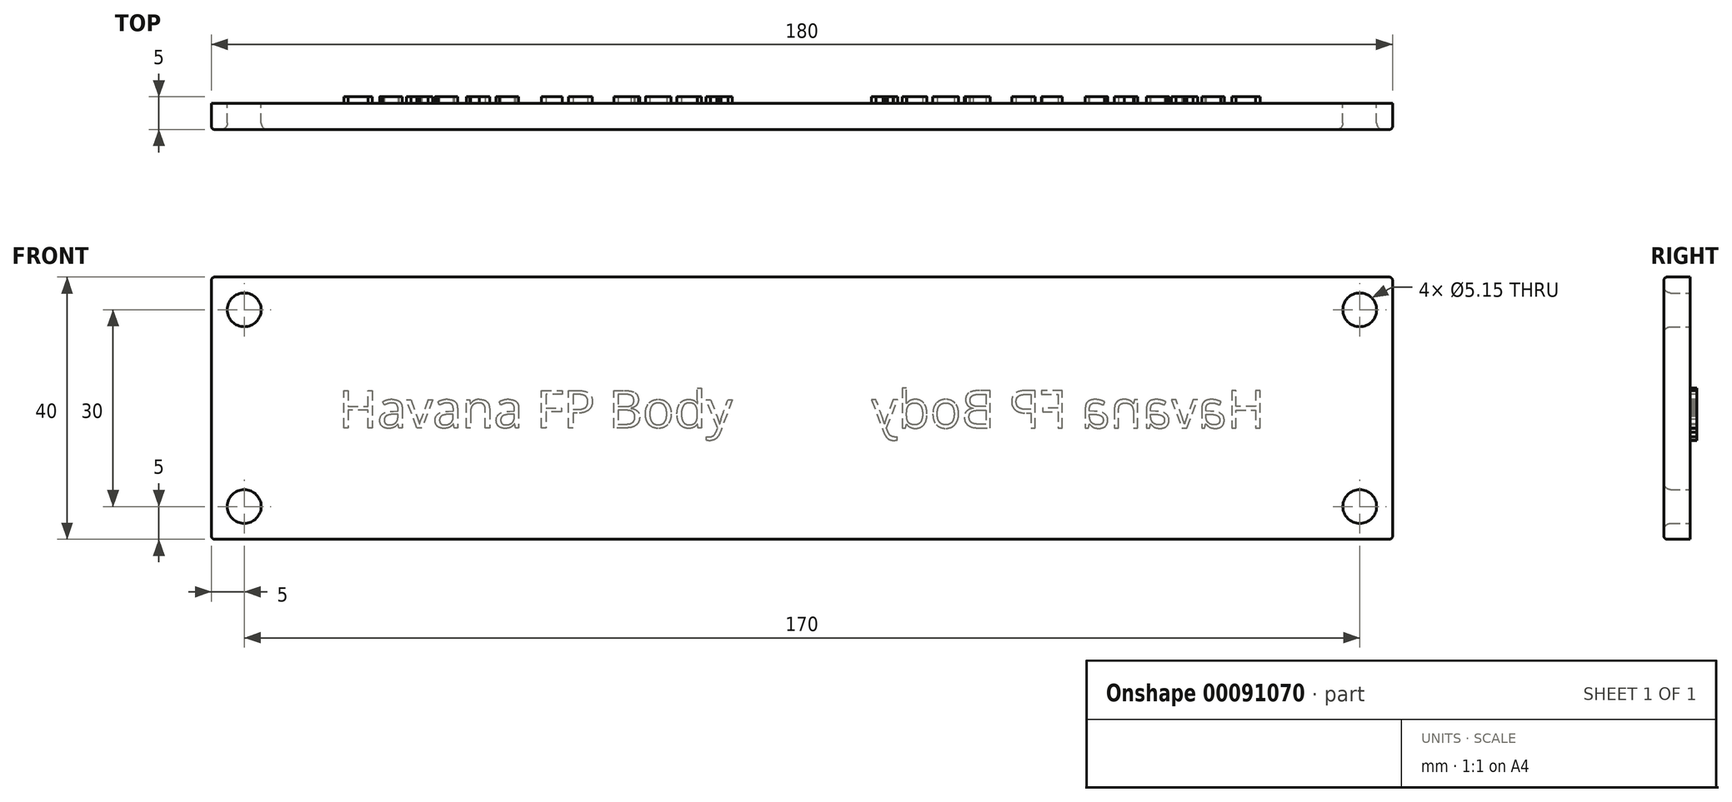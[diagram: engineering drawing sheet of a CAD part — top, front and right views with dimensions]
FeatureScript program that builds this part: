
annotation { "Feature Type Name" : "Feature", "Feature Type Description" : "" }
export const myFeature = defineFeature(function(context is Context, id is Id, definition is map)
    precondition{}
    {
        {
            var Q0;
            Q0=qCreatedBy(makeId("Front.planeOp"),FACE);
            var sketch = newSketch(context, id + "F0", { "sketchPlane" : qUnion([Q0])});
            skLineSegment(sketch, "E0.bottom", {"start": v(-90, -20) * mm, "end": v(90, -20) * mm});
            skLineSegment(sketch, "E0.top", {"start": v(-90, 20) * mm, "end": v(90, 20) * mm});
            skLineSegment(sketch, "E0.left", {"start": v(-90, -20) * mm, "end": v(-90, 20) * mm});
            skLineSegment(sketch, "E0.right", {"start": v(90, -20) * mm, "end": v(90, 20) * mm});
            skPoint(sketch, "E0.middle", {"position": v(0, 0) * mm});
            skCircle(sketch, "E1", {"center": v(-85, 15) * mm, "radius": 2.58 * mm});
            skPoint(sketch, "E2.start.orphan", {"position": v(-90, 0) * mm});
            skPoint(sketch, "E3.orphan", {"position": v(0, 20) * mm});
            skPoint(sketch, "E4.end.orphan", {"position": v(0, -20) * mm});
            skLineSegment(sketch, "E5", {"start": v(-90, 0) * mm, "end": v(0, 0) * mm, "construction": true});
            skLineSegment(sketch, "E6", {"start": v(0, 20) * mm, "end": v(0, -20) * mm, "construction": true});
            skCircle(sketch, "E7.MirrorC", {"center": v(-85, -15) * mm, "radius": 2.58 * mm});
            skCircle(sketch, "E8.MirrorC", {"center": v(85, 15) * mm, "radius": 2.58 * mm});
            skCircle(sketch, "E9.MirrorC", {"center": v(85, -15) * mm, "radius": 2.58 * mm});
            skSolve(sketch);
        }
        {
            var Q0;
            Q0=makeQuery(id+"F0.imprint","IMPRINT",FACE,{"disambiguationData":[TD([[makeQuery(id+"F0.imprint","IMPRINT",EDGE,{"derivedFrom":sQuery(id+"F0.wireOp",EDGE,"E0.bottom")}),1.0]])]});
            extrude(context, id + "F1", {"entities" : qUnion([Q0]), "depth" : 4 * mm});
        }
        {
            var Q0;
            Q0=makeQuery(id+"F1.opExtrude","CAP_EDGE",EDGE,{"disambiguationData":[OSD([sQuery(id+"F0.wireOp",EDGE,"E1")])],"isStart":false});
            var Q1;
            Q1=makeQuery(id+"F1.opExtrude","CAP_EDGE",EDGE,{"disambiguationData":[OSD([sQuery(id+"F0.wireOp",EDGE,"f5b72a5b-8583-449a-bdbf-9ac5a681e1fd0.MirrorC")])],"isStart":false});
            var Q2;
            Q2=makeQuery(id+"F1.opExtrude","CAP_EDGE",EDGE,{"disambiguationData":[OSD([sQuery(id+"F0.wireOp",EDGE,"2623e306-60f4-4522-aa65-1e3e8c2cf5b60.MirrorC")])],"isStart":false});
            var Q3;
            Q3=makeQuery(id+"F1.opExtrude","CAP_EDGE",EDGE,{"disambiguationData":[OSD([sQuery(id+"F0.wireOp",EDGE,"be81a34d-1d50-4ce7-a7a8-4484a1701fac0.MirrorC")])],"isStart":false});
            var Q4;
            Q4=makeQuery(id+"F1.opExtrude","CAP_EDGE",EDGE,{"disambiguationData":[OSD([sQuery(id+"F0.wireOp",EDGE,"E7.MirrorC")])],"isStart":false});
            var Q5;
            Q5=makeQuery(id+"F1.opExtrude","CAP_EDGE",EDGE,{"disambiguationData":[OSD([sQuery(id+"F0.wireOp",EDGE,"E8.MirrorC")])],"isStart":false});
            var Q6;
            Q6=makeQuery(id+"F1.opExtrude","CAP_EDGE",EDGE,{"disambiguationData":[OSD([sQuery(id+"F0.wireOp",EDGE,"E9.MirrorC")])],"isStart":false});
            fillet(context, id + "F2", {"entities" : qUnion([Q0, Q1, Q2, Q3, Q4, Q5, Q6]), "radius" : 1 * mm, "tangentPropagation" : true, "allowEdgeOverflow" : false});
        }
        {
            var Q0;
            Q0=makeQuery(id+"F1.opExtrude","CAP_EDGE",EDGE,{"disambiguationData":[OSD([sQuery(id+"F0.wireOp",EDGE,"E0.top")])],"isStart":false});
            var Q1;
            Q1=makeQuery(id+"F1.opExtrude","CAP_EDGE",EDGE,{"disambiguationData":[OSD([sQuery(id+"F0.wireOp",EDGE,"E0.left")])],"isStart":false});
            var Q2;
            Q2=makeQuery(id+"F1.opExtrude","CAP_EDGE",EDGE,{"disambiguationData":[OSD([sQuery(id+"F0.wireOp",EDGE,"E0.bottom")])],"isStart":false});
            var Q3;
            Q3=makeQuery(id+"F1.opExtrude","CAP_EDGE",EDGE,{"disambiguationData":[OSD([sQuery(id+"F0.wireOp",EDGE,"E0.right")])],"isStart":false});
            var Q4;
            Q4=makeQuery(id+"F1.opExtrude","SWEPT_EDGE",EDGE,{"disambiguationData":[OSD([sQuery(id+"F0.wireOp",EDGE,"E0.top"),sQuery(id+"F0.wireOp",EDGE,"E0.left")])]});
            var Q5;
            Q5=makeQuery(id+"F1.opExtrude","SWEPT_EDGE",EDGE,{"disambiguationData":[OSD([sQuery(id+"F0.wireOp",EDGE,"E0.bottom"),sQuery(id+"F0.wireOp",EDGE,"E0.left")])]});
            var Q6;
            Q6=makeQuery(id+"F1.opExtrude","SWEPT_EDGE",EDGE,{"disambiguationData":[OSD([sQuery(id+"F0.wireOp",EDGE,"E0.top"),sQuery(id+"F0.wireOp",EDGE,"E0.right")])]});
            var Q7;
            Q7=makeQuery(id+"F1.opExtrude","SWEPT_EDGE",EDGE,{"disambiguationData":[OSD([sQuery(id+"F0.wireOp",EDGE,"E0.bottom"),sQuery(id+"F0.wireOp",EDGE,"E0.right")])]});
            fillet(context, id + "F3", {"entities" : qUnion([Q0, Q1, Q2, Q3, Q4, Q5, Q6, Q7]), "radius" : .5 * mm, "tangentPropagation" : true, "allowEdgeOverflow" : false});
        }
        {
            var Q0;
            Q0=makeQuery(id+"F1.opExtrude","CAP_FACE",FACE,{"disambiguationData":[OSD([sQuery(id+"F0.wireOp",EDGE,"E0.bottom"),sQuery(id+"F0.wireOp",EDGE,"E0.top"),sQuery(id+"F0.wireOp",EDGE,"E0.left"),sQuery(id+"F0.wireOp",EDGE,"E0.right"),sQuery(id+"F0.wireOp",EDGE,"E1"),sQuery(id+"F0.wireOp",EDGE,"E7.MirrorC"),sQuery(id+"F0.wireOp",EDGE,"E8.MirrorC"),sQuery(id+"F0.wireOp",EDGE,"E9.MirrorC")])],"isStart":true});
            var sketch = newSketch(context, id + "F4", { "sketchPlane" : qUnion([Q0])});
            skText(sketch, "E10", { "text": "Havana FP Body", "fontName": "OpenSans-Regular.ttf"});
            skLineSegment(sketch, "E11", {"start": v(0, 20) * mm, "end": v(0, -20) * mm, "construction": true});
            const initialGuessF4  = {"E10": [-0.0706, -0.003, 1, 0, 0.00574]};
            skSetInitialGuess(sketch, initialGuessF4);
            skSolve(sketch);
        }
        {
            var Q0;
            Q0=qSketchRegion(id+"F4",true);
            extrude(context, id + "F5", {"entities" : qUnion([Q0]), "operationType" : NewBodyOperationType.ADD, "depth" : 1 * mm});
        }
        {
            var Q0;
            Q0=makeQuery(id+"F1.opExtrude","SWEPT_BODY",BODY,{"disambiguationData":[OSD([sQuery(id+"F0.wireOp",EDGE,"E0.bottom"),sQuery(id+"F0.wireOp",EDGE,"E0.top"),sQuery(id+"F0.wireOp",EDGE,"E0.left"),sQuery(id+"F0.wireOp",EDGE,"E0.right"),sQuery(id+"F0.wireOp",EDGE,"E1"),sQuery(id+"F0.wireOp",EDGE,"E7.MirrorC"),sQuery(id+"F0.wireOp",EDGE,"E8.MirrorC"),sQuery(id+"F0.wireOp",EDGE,"E9.MirrorC")])]});
            var Q1;
            Q1=makeQuery(id+"F5.opExtrude","SWEPT_FACE",FACE,{"disambiguationData":[OSD([sQuery(id+"F4.wireOp",EDGE,"E10.sketch_text.stroke-94")])]});
            var Q2;
            Q2=makeQuery(id+"F5.opExtrude","SWEPT_FACE",FACE,{"disambiguationData":[OSD([sQuery(id+"F4.wireOp",EDGE,"E10.sketch_text.stroke-169")])]});
            var Q3;
            Q3=makeQuery(id+"F5.opExtrude","SWEPT_FACE",FACE,{"disambiguationData":[OSD([sQuery(id+"F4.wireOp",EDGE,"E10.sketch_text.stroke-185")])]});
            var Q4;
            Q4=makeQuery(id+"F5.opExtrude","SWEPT_FACE",FACE,{"disambiguationData":[OSD([sQuery(id+"F4.wireOp",EDGE,"E10.sketch_text.stroke-125")])]});
            var Q5;
            Q5=makeQuery(id+"F5.opExtrude","SWEPT_FACE",FACE,{"disambiguationData":[OSD([sQuery(id+"F4.wireOp",EDGE,"E10.sketch_text.stroke-155")])]});
            var Q6;
            Q6=makeQuery(id+"F5.opExtrude","SWEPT_FACE",FACE,{"disambiguationData":[OSD([sQuery(id+"F4.wireOp",EDGE,"E10.sketch_text.stroke-65")])]});
            var Q7;
            Q7=makeQuery(id+"F5.opExtrude","SWEPT_FACE",FACE,{"disambiguationData":[OSD([sQuery(id+"F4.wireOp",EDGE,"E10.sketch_text.stroke-81")])]});
            var Q8;
            Q8=makeQuery(id+"F5.opExtrude","SWEPT_FACE",FACE,{"disambiguationData":[OSD([sQuery(id+"F4.wireOp",EDGE,"E10.sketch_text.stroke-67")])]});
            var Q9;
            Q9=makeQuery(id+"F5.opExtrude","SWEPT_FACE",FACE,{"disambiguationData":[OSD([sQuery(id+"F4.wireOp",EDGE,"E10.sketch_text.stroke-99")])]});
            var Q10;
            Q10=makeQuery(id+"F5.opExtrude","SWEPT_FACE",FACE,{"disambiguationData":[OSD([sQuery(id+"F4.wireOp",EDGE,"E10.sketch_text.stroke-127")])]});
            var Q11;
            Q11=makeQuery(id+"F5.opExtrude","SWEPT_FACE",FACE,{"disambiguationData":[OSD([sQuery(id+"F4.wireOp",EDGE,"E10.sketch_text.stroke-10")])]});
            var Q12;
            Q12=makeQuery(id+"F5.opExtrude","CAP_FACE",FACE,{"disambiguationData":[OSD([sQuery(id+"F4.wireOp",EDGE,"E10.sketch_text.stroke-9"),sQuery(id+"F4.wireOp",EDGE,"E10.sketch_text.stroke-10"),sQuery(id+"F4.wireOp",EDGE,"E10.sketch_text.stroke-11"),sQuery(id+"F4.wireOp",EDGE,"E10.sketch_text.stroke-12")])],"isStart":false});
            var Q13;
            Q13=makeQuery(id+"F5.opExtrude","SWEPT_FACE",FACE,{"disambiguationData":[OSD([sQuery(id+"F4.wireOp",EDGE,"E10.sketch_text.stroke-154")])]});
            var Q14;
            Q14=makeQuery(id+"F5.opExtrude","SWEPT_FACE",FACE,{"disambiguationData":[OSD([sQuery(id+"F4.wireOp",EDGE,"E10.sketch_text.stroke-1")])]});
            var Q15;
            Q15=makeQuery(id+"F5.opExtrude","CAP_FACE",FACE,{"disambiguationData":[OSD([sQuery(id+"F4.wireOp",EDGE,"E10.sketch_text.stroke-124"),sQuery(id+"F4.wireOp",EDGE,"E10.sketch_text.stroke-125"),sQuery(id+"F4.wireOp",EDGE,"E10.sketch_text.stroke-126"),sQuery(id+"F4.wireOp",EDGE,"E10.sketch_text.stroke-127"),sQuery(id+"F4.wireOp",EDGE,"E10.sketch_text.stroke-128"),sQuery(id+"F4.wireOp",EDGE,"E10.sketch_text.stroke-129"),sQuery(id+"F4.wireOp",EDGE,"E10.sketch_text.stroke-130"),sQuery(id+"F4.wireOp",EDGE,"E10.sketch_text.stroke-131"),sQuery(id+"F4.wireOp",EDGE,"E10.sketch_text.stroke-132"),sQuery(id+"F4.wireOp",EDGE,"E10.sketch_text.stroke-133"),sQuery(id+"F4.wireOp",EDGE,"E10.sketch_text.stroke-134"),sQuery(id+"F4.wireOp",EDGE,"E10.sketch_text.stroke-135"),sQuery(id+"F4.wireOp",EDGE,"E10.sketch_text.stroke-136"),sQuery(id+"F4.wireOp",EDGE,"E10.sketch_text.stroke-137"),sQuery(id+"F4.wireOp",EDGE,"E10.sketch_text.stroke-138")])],"isStart":false});
            var Q16;
            Q16=makeQuery(id+"F5.opExtrude","CAP_FACE",FACE,{"disambiguationData":[OSD([sQuery(id+"F4.wireOp",EDGE,"E10.sketch_text.stroke-34"),sQuery(id+"F4.wireOp",EDGE,"E10.sketch_text.stroke-35"),sQuery(id+"F4.wireOp",EDGE,"E10.sketch_text.stroke-36"),sQuery(id+"F4.wireOp",EDGE,"E10.sketch_text.stroke-37"),sQuery(id+"F4.wireOp",EDGE,"E10.sketch_text.stroke-38"),sQuery(id+"F4.wireOp",EDGE,"E10.sketch_text.stroke-39"),sQuery(id+"F4.wireOp",EDGE,"E10.sketch_text.stroke-40"),sQuery(id+"F4.wireOp",EDGE,"E10.sketch_text.stroke-41"),sQuery(id+"F4.wireOp",EDGE,"E10.sketch_text.stroke-42"),sQuery(id+"F4.wireOp",EDGE,"E10.sketch_text.stroke-43"),sQuery(id+"F4.wireOp",EDGE,"E10.sketch_text.stroke-44"),sQuery(id+"F4.wireOp",EDGE,"E10.sketch_text.stroke-45"),sQuery(id+"F4.wireOp",EDGE,"E10.sketch_text.stroke-46"),sQuery(id+"F4.wireOp",EDGE,"E10.sketch_text.stroke-47"),sQuery(id+"F4.wireOp",EDGE,"E10.sketch_text.stroke-48"),sQuery(id+"F4.wireOp",EDGE,"E10.sketch_text.stroke-49"),sQuery(id+"F4.wireOp",EDGE,"E10.sketch_text.stroke-50"),sQuery(id+"F4.wireOp",EDGE,"E10.sketch_text.stroke-51"),sQuery(id+"F4.wireOp",EDGE,"E10.sketch_text.stroke-52"),sQuery(id+"F4.wireOp",EDGE,"E10.sketch_text.stroke-53"),sQuery(id+"F4.wireOp",EDGE,"E10.sketch_text.stroke-54"),sQuery(id+"F4.wireOp",EDGE,"E10.sketch_text.stroke-55"),sQuery(id+"F4.wireOp",EDGE,"E10.sketch_text.stroke-56"),sQuery(id+"F4.wireOp",EDGE,"E10.sketch_text.stroke-57"),sQuery(id+"F4.wireOp",EDGE,"E10.sketch_text.stroke-58"),sQuery(id+"F4.wireOp",EDGE,"E10.sketch_text.stroke-59"),sQuery(id+"F4.wireOp",EDGE,"E10.sketch_text.stroke-60")])],"isStart":false});
            var Q17;
            Q17=makeQuery(id+"F5.opExtrude","SWEPT_FACE",FACE,{"disambiguationData":[OSD([sQuery(id+"F4.wireOp",EDGE,"E10.sketch_text.stroke-50")])]});
            var Q18;
            Q18=makeQuery(id+"F5.opExtrude","SWEPT_FACE",FACE,{"disambiguationData":[OSD([sQuery(id+"F4.wireOp",EDGE,"E10.sketch_text.stroke-2")])]});
            var Q19;
            Q19=makeQuery(id+"F5.opExtrude","SWEPT_FACE",FACE,{"disambiguationData":[OSD([sQuery(id+"F4.wireOp",EDGE,"E10.sketch_text.stroke-3")])]});
            var Q20;
            Q20=makeQuery(id+"F5.opExtrude","SWEPT_FACE",FACE,{"disambiguationData":[OSD([sQuery(id+"F4.wireOp",EDGE,"E10.sketch_text.stroke-5")])]});
            var Q21;
            Q21=makeQuery(id+"F5.opExtrude","SWEPT_FACE",FACE,{"disambiguationData":[OSD([sQuery(id+"F4.wireOp",EDGE,"E10.sketch_text.stroke-8")])]});
            var Q22;
            Q22=makeQuery(id+"F5.opExtrude","SWEPT_FACE",FACE,{"disambiguationData":[OSD([sQuery(id+"F4.wireOp",EDGE,"E10.sketch_text.stroke-98")])]});
            var Q23;
            Q23=makeQuery(id+"F5.opExtrude","SWEPT_FACE",FACE,{"disambiguationData":[OSD([sQuery(id+"F4.wireOp",EDGE,"E10.sketch_text.stroke-66")])]});
            var Q24;
            Q24=makeQuery(id+"F5.opExtrude","SWEPT_FACE",FACE,{"disambiguationData":[OSD([sQuery(id+"F4.wireOp",EDGE,"E10.sketch_text.stroke-153")])]});
            var Q25;
            Q25=makeQuery(id+"F5.opExtrude","SWEPT_FACE",FACE,{"disambiguationData":[OSD([sQuery(id+"F4.wireOp",EDGE,"E10.sketch_text.stroke-126")])]});
            var Q26;
            Q26=makeQuery(id+"F5.opExtrude","SWEPT_FACE",FACE,{"disambiguationData":[OSD([sQuery(id+"F4.wireOp",EDGE,"E10.sketch_text.stroke-183")])]});
            var Q27;
            Q27=makeQuery(id+"F5.opExtrude","SWEPT_FACE",FACE,{"disambiguationData":[OSD([sQuery(id+"F4.wireOp",EDGE,"E10.sketch_text.stroke-109")])]});
            var Q28;
            Q28=makeQuery(id+"F5.opExtrude","SWEPT_FACE",FACE,{"disambiguationData":[OSD([sQuery(id+"F4.wireOp",EDGE,"E10.sketch_text.stroke-186")])]});
            var Q29;
            Q29=makeQuery(id+"F5.opExtrude","SWEPT_FACE",FACE,{"disambiguationData":[OSD([sQuery(id+"F4.wireOp",EDGE,"E10.sketch_text.stroke-79")])]});
            var Q30;
            Q30=makeQuery(id+"F5.opExtrude","SWEPT_FACE",FACE,{"disambiguationData":[OSD([sQuery(id+"F4.wireOp",EDGE,"E10.sketch_text.stroke-110")])]});
            var Q31;
            Q31=makeQuery(id+"F5.opExtrude","SWEPT_FACE",FACE,{"disambiguationData":[OSD([sQuery(id+"F4.wireOp",EDGE,"E10.sketch_text.stroke-38")])]});
            var Q32;
            Q32=makeQuery(id+"F5.opExtrude","SWEPT_FACE",FACE,{"disambiguationData":[OSD([sQuery(id+"F4.wireOp",EDGE,"E10.sketch_text.stroke-24")])]});
            var Q33;
            Q33=makeQuery(id+"F5.opExtrude","SWEPT_FACE",FACE,{"disambiguationData":[OSD([sQuery(id+"F4.wireOp",EDGE,"E10.sketch_text.stroke-12")])]});
            var Q34;
            Q34=makeQuery(id+"F5.opExtrude","SWEPT_FACE",FACE,{"disambiguationData":[OSD([sQuery(id+"F4.wireOp",EDGE,"E10.sketch_text.stroke-100")])]});
            var Q35;
            Q35=makeQuery(id+"F5.opExtrude","SWEPT_FACE",FACE,{"disambiguationData":[OSD([sQuery(id+"F4.wireOp",EDGE,"E10.sketch_text.stroke-158")])]});
            var Q36;
            Q36=makeQuery(id+"F5.opExtrude","SWEPT_FACE",FACE,{"disambiguationData":[OSD([sQuery(id+"F4.wireOp",EDGE,"E10.sketch_text.stroke-142")])]});
            var Q37;
            Q37=makeQuery(id+"F5.opExtrude","SWEPT_FACE",FACE,{"disambiguationData":[OSD([sQuery(id+"F4.wireOp",EDGE,"E10.sketch_text.stroke-54")])]});
            var Q38;
            Q38=makeQuery(id+"F5.opExtrude","SWEPT_FACE",FACE,{"disambiguationData":[OSD([sQuery(id+"F4.wireOp",EDGE,"E10.sketch_text.stroke-25")])]});
            var Q39;
            Q39=makeQuery(id+"F5.opExtrude","SWEPT_FACE",FACE,{"disambiguationData":[OSD([sQuery(id+"F4.wireOp",EDGE,"E10.sketch_text.stroke-101")])]});
            var Q40;
            Q40=makeQuery(id+"F5.opExtrude","SWEPT_FACE",FACE,{"disambiguationData":[OSD([sQuery(id+"F4.wireOp",EDGE,"E10.sketch_text.stroke-69")])]});
            var Q41;
            Q41=makeQuery(id+"F5.opExtrude","SWEPT_FACE",FACE,{"disambiguationData":[OSD([sQuery(id+"F4.wireOp",EDGE,"E10.sketch_text.stroke-159")])]});
            var Q42;
            Q42=makeQuery(id+"F5.opExtrude","SWEPT_FACE",FACE,{"disambiguationData":[OSD([sQuery(id+"F4.wireOp",EDGE,"E10.sketch_text.stroke-85")])]});
            var Q43;
            Q43=makeQuery(id+"F5.opExtrude","SWEPT_FACE",FACE,{"disambiguationData":[OSD([sQuery(id+"F4.wireOp",EDGE,"E10.sketch_text.stroke-173")])]});
            var Q44;
            Q44=makeQuery(id+"F5.opExtrude","SWEPT_FACE",FACE,{"disambiguationData":[OSD([sQuery(id+"F4.wireOp",EDGE,"E10.sketch_text.stroke-40")])]});
            var Q45;
            Q45=makeQuery(id+"F5.opExtrude","SWEPT_FACE",FACE,{"disambiguationData":[OSD([sQuery(id+"F4.wireOp",EDGE,"E10.sketch_text.stroke-102")])]});
            var Q46;
            Q46=makeQuery(id+"F5.opExtrude","SWEPT_FACE",FACE,{"disambiguationData":[OSD([sQuery(id+"F4.wireOp",EDGE,"E10.sketch_text.stroke-86")])]});
            var Q47;
            Q47=makeQuery(id+"F5.opExtrude","SWEPT_FACE",FACE,{"disambiguationData":[OSD([sQuery(id+"F4.wireOp",EDGE,"E10.sketch_text.stroke-130")])]});
            var Q48;
            Q48=makeQuery(id+"F5.opExtrude","SWEPT_FACE",FACE,{"disambiguationData":[OSD([sQuery(id+"F4.wireOp",EDGE,"E10.sketch_text.stroke-103")])]});
            var Q49;
            Q49=makeQuery(id+"F5.opExtrude","SWEPT_FACE",FACE,{"disambiguationData":[OSD([sQuery(id+"F4.wireOp",EDGE,"E10.sketch_text.stroke-87")])]});
            var Q50;
            Q50=makeQuery(id+"F5.opExtrude","SWEPT_FACE",FACE,{"disambiguationData":[OSD([sQuery(id+"F4.wireOp",EDGE,"E10.sketch_text.stroke-145")])]});
            var Q51;
            Q51=makeQuery(id+"F5.opExtrude","SWEPT_FACE",FACE,{"disambiguationData":[OSD([sQuery(id+"F4.wireOp",EDGE,"E10.sketch_text.stroke-131")])]});
            var Q52;
            Q52=makeQuery(id+"F5.opExtrude","SWEPT_FACE",FACE,{"disambiguationData":[OSD([sQuery(id+"F4.wireOp",EDGE,"E10.sketch_text.stroke-28")])]});
            var Q53;
            Q53=makeQuery(id+"F5.opExtrude","SWEPT_FACE",FACE,{"disambiguationData":[OSD([sQuery(id+"F4.wireOp",EDGE,"E10.sketch_text.stroke-14")])]});
            var Q54;
            Q54=makeQuery(id+"F5.opExtrude","SWEPT_FACE",FACE,{"disambiguationData":[OSD([sQuery(id+"F4.wireOp",EDGE,"E10.sketch_text.stroke-88")])]});
            var Q55;
            Q55=makeQuery(id+"F5.opExtrude","SWEPT_FACE",FACE,{"disambiguationData":[OSD([sQuery(id+"F4.wireOp",EDGE,"E10.sketch_text.stroke-162")])]});
            var Q56;
            Q56=makeQuery(id+"F5.opExtrude","SWEPT_FACE",FACE,{"disambiguationData":[OSD([sQuery(id+"F4.wireOp",EDGE,"E10.sketch_text.stroke-176")])]});
            var Q57;
            Q57=makeQuery(id+"F5.opExtrude","SWEPT_FACE",FACE,{"disambiguationData":[OSD([sQuery(id+"F4.wireOp",EDGE,"E10.sketch_text.stroke-73")])]});
            var Q58;
            Q58=makeQuery(id+"F5.opExtrude","SWEPT_FACE",FACE,{"disambiguationData":[OSD([sQuery(id+"F4.wireOp",EDGE,"E10.sketch_text.stroke-59")])]});
            var Q59;
            Q59=makeQuery(id+"F5.opExtrude","SWEPT_FACE",FACE,{"disambiguationData":[OSD([sQuery(id+"F4.wireOp",EDGE,"E10.sketch_text.stroke-133")])]});
            var Q60;
            Q60=makeQuery(id+"F5.opExtrude","SWEPT_FACE",FACE,{"disambiguationData":[OSD([sQuery(id+"F4.wireOp",EDGE,"E10.sketch_text.stroke-119")])]});
            var Q61;
            Q61=makeQuery(id+"F5.opExtrude","SWEPT_FACE",FACE,{"disambiguationData":[OSD([sQuery(id+"F4.wireOp",EDGE,"E10.sketch_text.stroke-74")])]});
            var Q62;
            Q62=makeQuery(id+"F5.opExtrude","SWEPT_FACE",FACE,{"disambiguationData":[OSD([sQuery(id+"F4.wireOp",EDGE,"E10.sketch_text.stroke-44")])]});
            var Q63;
            Q63=makeQuery(id+"F5.opExtrude","SWEPT_FACE",FACE,{"disambiguationData":[OSD([sQuery(id+"F4.wireOp",EDGE,"E10.sketch_text.stroke-120")])]});
            var Q64;
            Q64=makeQuery(id+"F5.opExtrude","SWEPT_FACE",FACE,{"disambiguationData":[OSD([sQuery(id+"F4.wireOp",EDGE,"E10.sketch_text.stroke-90")])]});
            var Q65;
            Q65=makeQuery(id+"F5.opExtrude","SWEPT_FACE",FACE,{"disambiguationData":[OSD([sQuery(id+"F4.wireOp",EDGE,"E10.sketch_text.stroke-178")])]});
            var Q66;
            Q66=makeQuery(id+"F5.opExtrude","SWEPT_FACE",FACE,{"disambiguationData":[OSD([sQuery(id+"F4.wireOp",EDGE,"E10.sketch_text.stroke-45")])]});
            var Q67;
            Q67=makeQuery(id+"F5.opExtrude","SWEPT_FACE",FACE,{"disambiguationData":[OSD([sQuery(id+"F4.wireOp",EDGE,"E10.sketch_text.stroke-31")])]});
            var Q68;
            Q68=makeQuery(id+"F5.opExtrude","SWEPT_FACE",FACE,{"disambiguationData":[OSD([sQuery(id+"F4.wireOp",EDGE,"E10.sketch_text.stroke-135")])]});
            var Q69;
            Q69=makeQuery(id+"F5.opExtrude","SWEPT_FACE",FACE,{"disambiguationData":[OSD([sQuery(id+"F4.wireOp",EDGE,"E10.sketch_text.stroke-179")])]});
            var Q70;
            Q70=makeQuery(id+"F5.opExtrude","SWEPT_FACE",FACE,{"disambiguationData":[OSD([sQuery(id+"F4.wireOp",EDGE,"E10.sketch_text.stroke-165")])]});
            var Q71;
            Q71=makeQuery(id+"F5.opExtrude","SWEPT_FACE",FACE,{"disambiguationData":[OSD([sQuery(id+"F4.wireOp",EDGE,"E10.sketch_text.stroke-149")])]});
            var Q72;
            Q72=makeQuery(id+"F5.opExtrude","SWEPT_FACE",FACE,{"disambiguationData":[OSD([sQuery(id+"F4.wireOp",EDGE,"E10.sketch_text.stroke-136")])]});
            var Q73;
            Q73=makeQuery(id+"F5.opExtrude","SWEPT_FACE",FACE,{"disambiguationData":[OSD([sQuery(id+"F4.wireOp",EDGE,"E10.sketch_text.stroke-122")])]});
            var Q74;
            Q74=makeQuery(id+"F5.opExtrude","SWEPT_FACE",FACE,{"disambiguationData":[OSD([sQuery(id+"F4.wireOp",EDGE,"E10.sketch_text.stroke-106")])]});
            var Q75;
            Q75=makeQuery(id+"F5.opExtrude","SWEPT_FACE",FACE,{"disambiguationData":[OSD([sQuery(id+"F4.wireOp",EDGE,"E10.sketch_text.stroke-180")])]});
            var Q76;
            Q76=makeQuery(id+"F5.opExtrude","SWEPT_FACE",FACE,{"disambiguationData":[OSD([sQuery(id+"F4.wireOp",EDGE,"E10.sketch_text.stroke-166")])]});
            var Q77;
            Q77=makeQuery(id+"F5.opExtrude","SWEPT_FACE",FACE,{"disambiguationData":[OSD([sQuery(id+"F4.wireOp",EDGE,"E10.sketch_text.stroke-150")])]});
            var Q78;
            Q78=makeQuery(id+"F5.opExtrude","SWEPT_FACE",FACE,{"disambiguationData":[OSD([sQuery(id+"F4.wireOp",EDGE,"E10.sketch_text.stroke-76")])]});
            var Q79;
            Q79=makeQuery(id+"F5.opExtrude","SWEPT_FACE",FACE,{"disambiguationData":[OSD([sQuery(id+"F4.wireOp",EDGE,"E10.sketch_text.stroke-32")])]});
            var Q80;
            Q80=makeQuery(id+"F5.opExtrude","SWEPT_FACE",FACE,{"disambiguationData":[OSD([sQuery(id+"F4.wireOp",EDGE,"E10.sketch_text.stroke-181")])]});
            var Q81;
            Q81=makeQuery(id+"F5.opExtrude","SWEPT_FACE",FACE,{"disambiguationData":[OSD([sQuery(id+"F4.wireOp",EDGE,"E10.sketch_text.stroke-47")])]});
            var Q82;
            Q82=makeQuery(id+"F5.opExtrude","SWEPT_FACE",FACE,{"disambiguationData":[OSD([sQuery(id+"F4.wireOp",EDGE,"E10.sketch_text.stroke-123")])]});
            var Q83;
            Q83=makeQuery(id+"F5.opExtrude","SWEPT_FACE",FACE,{"disambiguationData":[OSD([sQuery(id+"F4.wireOp",EDGE,"E10.sketch_text.stroke-107")])]});
            var Q84;
            Q84=makeQuery(id+"F5.opExtrude","SWEPT_FACE",FACE,{"disambiguationData":[OSD([sQuery(id+"F4.wireOp",EDGE,"E10.sketch_text.stroke-48")])]});
            var Q85;
            Q85=makeQuery(id+"F5.opExtrude","SWEPT_FACE",FACE,{"disambiguationData":[OSD([sQuery(id+"F4.wireOp",EDGE,"E10.sketch_text.stroke-124")])]});
            var Q86;
            Q86=makeQuery(id+"F5.opExtrude","SWEPT_FACE",FACE,{"disambiguationData":[OSD([sQuery(id+"F4.wireOp",EDGE,"E10.sketch_text.stroke-108")])]});
            var Q87;
            Q87=makeQuery(id+"F5.opExtrude","CAP_FACE",FACE,{"disambiguationData":[OSD([sQuery(id+"F4.wireOp",EDGE,"E10.sketch_text.stroke-139"),sQuery(id+"F4.wireOp",EDGE,"E10.sketch_text.stroke-140"),sQuery(id+"F4.wireOp",EDGE,"E10.sketch_text.stroke-141"),sQuery(id+"F4.wireOp",EDGE,"E10.sketch_text.stroke-142"),sQuery(id+"F4.wireOp",EDGE,"E10.sketch_text.stroke-143"),sQuery(id+"F4.wireOp",EDGE,"E10.sketch_text.stroke-144"),sQuery(id+"F4.wireOp",EDGE,"E10.sketch_text.stroke-145"),sQuery(id+"F4.wireOp",EDGE,"E10.sketch_text.stroke-146"),sQuery(id+"F4.wireOp",EDGE,"E10.sketch_text.stroke-147"),sQuery(id+"F4.wireOp",EDGE,"E10.sketch_text.stroke-148"),sQuery(id+"F4.wireOp",EDGE,"E10.sketch_text.stroke-149"),sQuery(id+"F4.wireOp",EDGE,"E10.sketch_text.stroke-150"),sQuery(id+"F4.wireOp",EDGE,"E10.sketch_text.stroke-151"),sQuery(id+"F4.wireOp",EDGE,"E10.sketch_text.stroke-152"),sQuery(id+"F4.wireOp",EDGE,"E10.sketch_text.stroke-153"),sQuery(id+"F4.wireOp",EDGE,"E10.sketch_text.stroke-154"),sQuery(id+"F4.wireOp",EDGE,"E10.sketch_text.stroke-155"),sQuery(id+"F4.wireOp",EDGE,"E10.sketch_text.stroke-156"),sQuery(id+"F4.wireOp",EDGE,"E10.sketch_text.stroke-157"),sQuery(id+"F4.wireOp",EDGE,"E10.sketch_text.stroke-158"),sQuery(id+"F4.wireOp",EDGE,"E10.sketch_text.stroke-159"),sQuery(id+"F4.wireOp",EDGE,"E10.sketch_text.stroke-160"),sQuery(id+"F4.wireOp",EDGE,"E10.sketch_text.stroke-161"),sQuery(id+"F4.wireOp",EDGE,"E10.sketch_text.stroke-162"),sQuery(id+"F4.wireOp",EDGE,"E10.sketch_text.stroke-163"),sQuery(id+"F4.wireOp",EDGE,"E10.sketch_text.stroke-164"),sQuery(id+"F4.wireOp",EDGE,"E10.sketch_text.stroke-165")])],"isStart":false});
            var Q88;
            Q88=makeQuery(id+"F5.opExtrude","CAP_FACE",FACE,{"disambiguationData":[OSD([sQuery(id+"F4.wireOp",EDGE,"E10.sketch_text.stroke-21"),sQuery(id+"F4.wireOp",EDGE,"E10.sketch_text.stroke-22"),sQuery(id+"F4.wireOp",EDGE,"E10.sketch_text.stroke-23"),sQuery(id+"F4.wireOp",EDGE,"E10.sketch_text.stroke-24"),sQuery(id+"F4.wireOp",EDGE,"E10.sketch_text.stroke-25"),sQuery(id+"F4.wireOp",EDGE,"E10.sketch_text.stroke-26"),sQuery(id+"F4.wireOp",EDGE,"E10.sketch_text.stroke-27"),sQuery(id+"F4.wireOp",EDGE,"E10.sketch_text.stroke-28"),sQuery(id+"F4.wireOp",EDGE,"E10.sketch_text.stroke-29"),sQuery(id+"F4.wireOp",EDGE,"E10.sketch_text.stroke-30"),sQuery(id+"F4.wireOp",EDGE,"E10.sketch_text.stroke-31"),sQuery(id+"F4.wireOp",EDGE,"E10.sketch_text.stroke-32"),sQuery(id+"F4.wireOp",EDGE,"E10.sketch_text.stroke-33")])],"isStart":false});
            var Q89;
            Q89=makeQuery(id+"F5.opExtrude","SWEPT_FACE",FACE,{"disambiguationData":[OSD([sQuery(id+"F4.wireOp",EDGE,"E10.sketch_text.stroke-113")])]});
            var Q90;
            Q90=makeQuery(id+"F5.opExtrude","SWEPT_FACE",FACE,{"disambiguationData":[OSD([sQuery(id+"F4.wireOp",EDGE,"E10.sketch_text.stroke-37")])]});
            var Q91;
            Q91=makeQuery(id+"F5.opExtrude","SWEPT_FACE",FACE,{"disambiguationData":[OSD([sQuery(id+"F4.wireOp",EDGE,"E10.sketch_text.stroke-187")])]});
            var Q92;
            Q92=makeQuery(id+"F5.opExtrude","SWEPT_FACE",FACE,{"disambiguationData":[OSD([sQuery(id+"F4.wireOp",EDGE,"E10.sketch_text.stroke-0")])]});
            var Q93;
            Q93=makeQuery(id+"F5.opExtrude","SWEPT_FACE",FACE,{"disambiguationData":[OSD([sQuery(id+"F4.wireOp",EDGE,"E10.sketch_text.stroke-4")])]});
            var Q94;
            Q94=makeQuery(id+"F5.opExtrude","SWEPT_FACE",FACE,{"disambiguationData":[OSD([sQuery(id+"F4.wireOp",EDGE,"E10.sketch_text.stroke-82")])]});
            var Q95;
            Q95=makeQuery(id+"F5.opExtrude","SWEPT_FACE",FACE,{"disambiguationData":[OSD([sQuery(id+"F4.wireOp",EDGE,"E10.sketch_text.stroke-52")])]});
            var Q96;
            Q96=makeQuery(id+"F5.opExtrude","SWEPT_FACE",FACE,{"disambiguationData":[OSD([sQuery(id+"F4.wireOp",EDGE,"E10.sketch_text.stroke-49")])]});
            var Q97;
            Q97=makeQuery(id+"F5.opExtrude","SWEPT_FACE",FACE,{"disambiguationData":[OSD([sQuery(id+"F4.wireOp",EDGE,"E10.sketch_text.stroke-63")])]});
            var Q98;
            Q98=makeQuery(id+"F5.opExtrude","SWEPT_FACE",FACE,{"disambiguationData":[OSD([sQuery(id+"F4.wireOp",EDGE,"E10.sketch_text.stroke-21")])]});
            var Q99;
            Q99=makeQuery(id+"F5.opExtrude","SWEPT_FACE",FACE,{"disambiguationData":[OSD([sQuery(id+"F4.wireOp",EDGE,"E10.sketch_text.stroke-128")])]});
            var Q100;
            Q100=makeQuery(id+"F5.opExtrude","SWEPT_FACE",FACE,{"disambiguationData":[OSD([sQuery(id+"F4.wireOp",EDGE,"E10.sketch_text.stroke-55")])]});
            var Q101;
            Q101=makeQuery(id+"F5.opExtrude","SWEPT_FACE",FACE,{"disambiguationData":[OSD([sQuery(id+"F4.wireOp",EDGE,"E10.sketch_text.stroke-26")])]});
            var Q102;
            Q102=makeQuery(id+"F5.opExtrude","SWEPT_FACE",FACE,{"disambiguationData":[OSD([sQuery(id+"F4.wireOp",EDGE,"E10.sketch_text.stroke-174")])]});
            var Q103;
            Q103=makeQuery(id+"F5.opExtrude","SWEPT_FACE",FACE,{"disambiguationData":[OSD([sQuery(id+"F4.wireOp",EDGE,"E10.sketch_text.stroke-104")])]});
            var Q104;
            Q104=makeQuery(id+"F5.opExtrude","SWEPT_FACE",FACE,{"disambiguationData":[OSD([sQuery(id+"F4.wireOp",EDGE,"E10.sketch_text.stroke-72")])]});
            var Q105;
            Q105=makeQuery(id+"F5.opExtrude","SWEPT_FACE",FACE,{"disambiguationData":[OSD([sQuery(id+"F4.wireOp",EDGE,"E10.sketch_text.stroke-132")])]});
            var Q106;
            Q106=makeQuery(id+"F5.opExtrude","SWEPT_FACE",FACE,{"disambiguationData":[OSD([sQuery(id+"F4.wireOp",EDGE,"E10.sketch_text.stroke-43")])]});
            var Q107;
            Q107=makeQuery(id+"F5.opExtrude","SWEPT_FACE",FACE,{"disambiguationData":[OSD([sQuery(id+"F4.wireOp",EDGE,"E10.sketch_text.stroke-15")])]});
            var Q108;
            Q108=makeQuery(id+"F5.opExtrude","SWEPT_FACE",FACE,{"disambiguationData":[OSD([sQuery(id+"F4.wireOp",EDGE,"E10.sketch_text.stroke-89")])]});
            var Q109;
            Q109=makeQuery(id+"F5.opExtrude","SWEPT_FACE",FACE,{"disambiguationData":[OSD([sQuery(id+"F4.wireOp",EDGE,"E10.sketch_text.stroke-163")])]});
            var Q110;
            Q110=makeQuery(id+"F5.opExtrude","SWEPT_FACE",FACE,{"disambiguationData":[OSD([sQuery(id+"F4.wireOp",EDGE,"E10.sketch_text.stroke-30")])]});
            var Q111;
            Q111=makeQuery(id+"F5.opExtrude","SWEPT_FACE",FACE,{"disambiguationData":[OSD([sQuery(id+"F4.wireOp",EDGE,"E10.sketch_text.stroke-134")])]});
            var Q112;
            Q112=makeQuery(id+"F5.opExtrude","SWEPT_FACE",FACE,{"disambiguationData":[OSD([sQuery(id+"F4.wireOp",EDGE,"E10.sketch_text.stroke-121")])]});
            var Q113;
            Q113=makeQuery(id+"F5.opExtrude","CAP_FACE",FACE,{"disambiguationData":[OSD([sQuery(id+"F4.wireOp",EDGE,"E10.sketch_text.stroke-105"),sQuery(id+"F4.wireOp",EDGE,"E10.sketch_text.stroke-106"),sQuery(id+"F4.wireOp",EDGE,"E10.sketch_text.stroke-107"),sQuery(id+"F4.wireOp",EDGE,"E10.sketch_text.stroke-108"),sQuery(id+"F4.wireOp",EDGE,"E10.sketch_text.stroke-109"),sQuery(id+"F4.wireOp",EDGE,"E10.sketch_text.stroke-110"),sQuery(id+"F4.wireOp",EDGE,"E10.sketch_text.stroke-111"),sQuery(id+"F4.wireOp",EDGE,"E10.sketch_text.stroke-112"),sQuery(id+"F4.wireOp",EDGE,"E10.sketch_text.stroke-113"),sQuery(id+"F4.wireOp",EDGE,"E10.sketch_text.stroke-114"),sQuery(id+"F4.wireOp",EDGE,"E10.sketch_text.stroke-115"),sQuery(id+"F4.wireOp",EDGE,"E10.sketch_text.stroke-116"),sQuery(id+"F4.wireOp",EDGE,"E10.sketch_text.stroke-117"),sQuery(id+"F4.wireOp",EDGE,"E10.sketch_text.stroke-118"),sQuery(id+"F4.wireOp",EDGE,"E10.sketch_text.stroke-119"),sQuery(id+"F4.wireOp",EDGE,"E10.sketch_text.stroke-120"),sQuery(id+"F4.wireOp",EDGE,"E10.sketch_text.stroke-121"),sQuery(id+"F4.wireOp",EDGE,"E10.sketch_text.stroke-122"),sQuery(id+"F4.wireOp",EDGE,"E10.sketch_text.stroke-123")])],"isStart":false});
            var Q114;
            Q114=makeQuery(id+"F5.opExtrude","SWEPT_FACE",FACE,{"disambiguationData":[OSD([sQuery(id+"F4.wireOp",EDGE,"E10.sketch_text.stroke-92")])]});
            var Q115;
            Q115=makeQuery(id+"F5.opExtrude","SWEPT_FACE",FACE,{"disambiguationData":[OSD([sQuery(id+"F4.wireOp",EDGE,"E10.sketch_text.stroke-46")])]});
            var Q116;
            Q116=makeQuery(id+"F5.opExtrude","CAP_FACE",FACE,{"disambiguationData":[OSD([sQuery(id+"F4.wireOp",EDGE,"E10.sketch_text.stroke-61"),sQuery(id+"F4.wireOp",EDGE,"E10.sketch_text.stroke-62"),sQuery(id+"F4.wireOp",EDGE,"E10.sketch_text.stroke-63"),sQuery(id+"F4.wireOp",EDGE,"E10.sketch_text.stroke-64"),sQuery(id+"F4.wireOp",EDGE,"E10.sketch_text.stroke-65"),sQuery(id+"F4.wireOp",EDGE,"E10.sketch_text.stroke-66"),sQuery(id+"F4.wireOp",EDGE,"E10.sketch_text.stroke-67"),sQuery(id+"F4.wireOp",EDGE,"E10.sketch_text.stroke-68"),sQuery(id+"F4.wireOp",EDGE,"E10.sketch_text.stroke-69"),sQuery(id+"F4.wireOp",EDGE,"E10.sketch_text.stroke-70"),sQuery(id+"F4.wireOp",EDGE,"E10.sketch_text.stroke-71"),sQuery(id+"F4.wireOp",EDGE,"E10.sketch_text.stroke-72"),sQuery(id+"F4.wireOp",EDGE,"E10.sketch_text.stroke-73"),sQuery(id+"F4.wireOp",EDGE,"E10.sketch_text.stroke-74"),sQuery(id+"F4.wireOp",EDGE,"E10.sketch_text.stroke-75"),sQuery(id+"F4.wireOp",EDGE,"E10.sketch_text.stroke-76"),sQuery(id+"F4.wireOp",EDGE,"E10.sketch_text.stroke-77"),sQuery(id+"F4.wireOp",EDGE,"E10.sketch_text.stroke-78"),sQuery(id+"F4.wireOp",EDGE,"E10.sketch_text.stroke-79"),sQuery(id+"F4.wireOp",EDGE,"E10.sketch_text.stroke-80"),sQuery(id+"F4.wireOp",EDGE,"E10.sketch_text.stroke-81"),sQuery(id+"F4.wireOp",EDGE,"E10.sketch_text.stroke-82"),sQuery(id+"F4.wireOp",EDGE,"E10.sketch_text.stroke-83"),sQuery(id+"F4.wireOp",EDGE,"E10.sketch_text.stroke-84"),sQuery(id+"F4.wireOp",EDGE,"E10.sketch_text.stroke-85"),sQuery(id+"F4.wireOp",EDGE,"E10.sketch_text.stroke-86"),sQuery(id+"F4.wireOp",EDGE,"E10.sketch_text.stroke-87"),sQuery(id+"F4.wireOp",EDGE,"E10.sketch_text.stroke-88"),sQuery(id+"F4.wireOp",EDGE,"E10.sketch_text.stroke-89"),sQuery(id+"F4.wireOp",EDGE,"E10.sketch_text.stroke-90"),sQuery(id+"F4.wireOp",EDGE,"E10.sketch_text.stroke-91"),sQuery(id+"F4.wireOp",EDGE,"E10.sketch_text.stroke-92"),sQuery(id+"F4.wireOp",EDGE,"E10.sketch_text.stroke-93"),sQuery(id+"F4.wireOp",EDGE,"E10.sketch_text.stroke-94"),sQuery(id+"F4.wireOp",EDGE,"E10.sketch_text.stroke-95"),sQuery(id+"F4.wireOp",EDGE,"E10.sketch_text.stroke-96"),sQuery(id+"F4.wireOp",EDGE,"E10.sketch_text.stroke-97"),sQuery(id+"F4.wireOp",EDGE,"E10.sketch_text.stroke-98"),sQuery(id+"F4.wireOp",EDGE,"E10.sketch_text.stroke-99"),sQuery(id+"F4.wireOp",EDGE,"E10.sketch_text.stroke-100"),sQuery(id+"F4.wireOp",EDGE,"E10.sketch_text.stroke-101"),sQuery(id+"F4.wireOp",EDGE,"E10.sketch_text.stroke-102"),sQuery(id+"F4.wireOp",EDGE,"E10.sketch_text.stroke-103"),sQuery(id+"F4.wireOp",EDGE,"E10.sketch_text.stroke-104")])],"isStart":false});
            var Q117;
            Q117=makeQuery(id+"F5.opExtrude","SWEPT_FACE",FACE,{"disambiguationData":[OSD([sQuery(id+"F4.wireOp",EDGE,"E10.sketch_text.stroke-33")])]});
            var Q118;
            Q118=makeQuery(id+"F5.opExtrude","SWEPT_FACE",FACE,{"disambiguationData":[OSD([sQuery(id+"F4.wireOp",EDGE,"E10.sketch_text.stroke-93")])]});
            var Q119;
            Q119=makeQuery(id+"F5.opExtrude","SWEPT_FACE",FACE,{"disambiguationData":[OSD([sQuery(id+"F4.wireOp",EDGE,"E10.sketch_text.stroke-34")])]});
            var Q120;
            Q120=makeQuery(id+"F5.opExtrude","SWEPT_FACE",FACE,{"disambiguationData":[OSD([sQuery(id+"F4.wireOp",EDGE,"E10.sketch_text.stroke-152")])]});
            var Q121;
            Q121=makeQuery(id+"F5.opExtrude","SWEPT_FACE",FACE,{"disambiguationData":[OSD([sQuery(id+"F4.wireOp",EDGE,"E10.sketch_text.stroke-51")])]});
            var Q122;
            Q122=makeQuery(id+"F5.opExtrude","SWEPT_FACE",FACE,{"disambiguationData":[OSD([sQuery(id+"F4.wireOp",EDGE,"E10.sketch_text.stroke-6")])]});
            var Q123;
            Q123=makeQuery(id+"F5.opExtrude","SWEPT_FACE",FACE,{"disambiguationData":[OSD([sQuery(id+"F4.wireOp",EDGE,"E10.sketch_text.stroke-7")])]});
            var Q124;
            Q124=makeQuery(id+"F5.opExtrude","SWEPT_FACE",FACE,{"disambiguationData":[OSD([sQuery(id+"F4.wireOp",EDGE,"E10.sketch_text.stroke-156")])]});
            var Q125;
            Q125=makeQuery(id+"F5.opExtrude","SWEPT_FACE",FACE,{"disambiguationData":[OSD([sQuery(id+"F4.wireOp",EDGE,"E10.sketch_text.stroke-112")])]});
            var Q126;
            Q126=makeQuery(id+"F5.boolean.opBoolean","SPLIT",FACE,{"disambiguationData":[TD([makeQuery(id+"F5.opExtrude","SWEPT_FACE",FACE,{"disambiguationData":[OSD([sQuery(id+"F4.wireOp",EDGE,"E10.sketch_text.stroke-182")])]})])],"derivedFrom":makeQuery(id+"F1.opExtrude","CAP_FACE",FACE,{"disambiguationData":[OSD([sQuery(id+"F0.wireOp",EDGE,"E0.bottom"),sQuery(id+"F0.wireOp",EDGE,"E0.top"),sQuery(id+"F0.wireOp",EDGE,"E0.left"),sQuery(id+"F0.wireOp",EDGE,"E0.right"),sQuery(id+"F0.wireOp",EDGE,"E1"),sQuery(id+"F0.wireOp",EDGE,"E7.MirrorC"),sQuery(id+"F0.wireOp",EDGE,"E8.MirrorC"),sQuery(id+"F0.wireOp",EDGE,"E9.MirrorC")])],"isStart":true})});
            var Q127;
            Q127=makeQuery(id+"F5.opExtrude","SWEPT_FACE",FACE,{"disambiguationData":[OSD([sQuery(id+"F4.wireOp",EDGE,"E10.sketch_text.stroke-96")])]});
            var Q128;
            Q128=makeQuery(id+"F5.opExtrude","SWEPT_FACE",FACE,{"disambiguationData":[OSD([sQuery(id+"F4.wireOp",EDGE,"E10.sketch_text.stroke-114")])]});
            var Q129;
            Q129=makeQuery(id+"F5.opExtrude","SWEPT_FACE",FACE,{"disambiguationData":[OSD([sQuery(id+"F4.wireOp",EDGE,"E10.sketch_text.stroke-39")])]});
            var Q130;
            Q130=makeQuery(id+"F5.opExtrude","SWEPT_FACE",FACE,{"disambiguationData":[OSD([sQuery(id+"F4.wireOp",EDGE,"E10.sketch_text.stroke-13")])]});
            var Q131;
            Q131=makeQuery(id+"F5.opExtrude","SWEPT_FACE",FACE,{"disambiguationData":[OSD([sQuery(id+"F4.wireOp",EDGE,"E10.sketch_text.stroke-115")])]});
            var Q132;
            Q132=makeQuery(id+"F5.opExtrude","SWEPT_FACE",FACE,{"disambiguationData":[OSD([sQuery(id+"F4.wireOp",EDGE,"E10.sketch_text.stroke-56")])]});
            var Q133;
            Q133=makeQuery(id+"F5.opExtrude","SWEPT_FACE",FACE,{"disambiguationData":[OSD([sQuery(id+"F4.wireOp",EDGE,"E10.sketch_text.stroke-144")])]});
            var Q134;
            Q134=makeQuery(id+"F5.opExtrude","SWEPT_FACE",FACE,{"disambiguationData":[OSD([sQuery(id+"F4.wireOp",EDGE,"E10.sketch_text.stroke-190")])]});
            var Q135;
            Q135=makeQuery(id+"F5.opExtrude","SWEPT_FACE",FACE,{"disambiguationData":[OSD([sQuery(id+"F4.wireOp",EDGE,"E10.sketch_text.stroke-116")])]});
            var Q136;
            Q136=makeQuery(id+"F5.opExtrude","SWEPT_FACE",FACE,{"disambiguationData":[OSD([sQuery(id+"F4.wireOp",EDGE,"E10.sketch_text.stroke-41")])]});
            var Q137;
            Q137=makeQuery(id+"F5.opExtrude","SWEPT_FACE",FACE,{"disambiguationData":[OSD([sQuery(id+"F4.wireOp",EDGE,"E10.sketch_text.stroke-161")])]});
            var Q138;
            Q138=makeQuery(id+"F5.opExtrude","SWEPT_FACE",FACE,{"disambiguationData":[OSD([sQuery(id+"F4.wireOp",EDGE,"E10.sketch_text.stroke-146")])]});
            var Q139;
            Q139=makeQuery(id+"F5.opExtrude","SWEPT_FACE",FACE,{"disambiguationData":[OSD([sQuery(id+"F4.wireOp",EDGE,"E10.sketch_text.stroke-58")])]});
            var Q140;
            Q140=makeQuery(id+"F5.opExtrude","SWEPT_FACE",FACE,{"disambiguationData":[OSD([sQuery(id+"F4.wireOp",EDGE,"E10.sketch_text.stroke-105")])]});
            var Q141;
            Q141=makeQuery(id+"F5.opExtrude","SWEPT_FACE",FACE,{"disambiguationData":[OSD([sQuery(id+"F4.wireOp",EDGE,"E10.sketch_text.stroke-177")])]});
            var Q142;
            Q142=makeQuery(id+"F5.opExtrude","SWEPT_FACE",FACE,{"disambiguationData":[OSD([sQuery(id+"F4.wireOp",EDGE,"E10.sketch_text.stroke-77")])]});
            var Q143;
            Q143=makeQuery(id+"F5.opExtrude","SWEPT_FACE",FACE,{"disambiguationData":[OSD([sQuery(id+"F4.wireOp",EDGE,"E10.sketch_text.stroke-138")])]});
            var Q144;
            Q144=makeQuery(id+"F5.opExtrude","SWEPT_FACE",FACE,{"disambiguationData":[OSD([sQuery(id+"F4.wireOp",EDGE,"E10.sketch_text.stroke-111")])]});
            var Q145;
            Q145=makeQuery(id+"F5.opExtrude","SWEPT_FACE",FACE,{"disambiguationData":[OSD([sQuery(id+"F4.wireOp",EDGE,"E10.sketch_text.stroke-53")])]});
            var Q146;
            Q146=makeQuery(id+"F5.opExtrude","SWEPT_FACE",FACE,{"disambiguationData":[OSD([sQuery(id+"F4.wireOp",EDGE,"E10.sketch_text.stroke-141")])]});
            var Q147;
            Q147=makeQuery(id+"F5.opExtrude","SWEPT_FACE",FACE,{"disambiguationData":[OSD([sQuery(id+"F4.wireOp",EDGE,"E10.sketch_text.stroke-157")])]});
            var Q148;
            Q148=makeQuery(id+"F5.opExtrude","SWEPT_FACE",FACE,{"disambiguationData":[OSD([sQuery(id+"F4.wireOp",EDGE,"E10.sketch_text.stroke-64")])]});
            var Q149;
            Q149=makeQuery(id+"F5.boolean.opBoolean","SPLIT",FACE,{"disambiguationData":[TD([makeQuery(id+"F5.opExtrude","SWEPT_FACE",FACE,{"disambiguationData":[OSD([sQuery(id+"F4.wireOp",EDGE,"E10.sketch_text.stroke-53")])]})])],"derivedFrom":makeQuery(id+"F1.opExtrude","CAP_FACE",FACE,{"disambiguationData":[OSD([sQuery(id+"F0.wireOp",EDGE,"E0.bottom"),sQuery(id+"F0.wireOp",EDGE,"E0.top"),sQuery(id+"F0.wireOp",EDGE,"E0.left"),sQuery(id+"F0.wireOp",EDGE,"E0.right"),sQuery(id+"F0.wireOp",EDGE,"E1"),sQuery(id+"F0.wireOp",EDGE,"E7.MirrorC"),sQuery(id+"F0.wireOp",EDGE,"E8.MirrorC"),sQuery(id+"F0.wireOp",EDGE,"E9.MirrorC")])],"isStart":true})});
            var Q150;
            Q150=makeQuery(id+"F5.opExtrude","SWEPT_FACE",FACE,{"disambiguationData":[OSD([sQuery(id+"F4.wireOp",EDGE,"E10.sketch_text.stroke-36")])]});
            var Q151;
            Q151=makeQuery(id+"F5.opExtrude","SWEPT_FACE",FACE,{"disambiguationData":[OSD([sQuery(id+"F4.wireOp",EDGE,"E10.sketch_text.stroke-22")])]});
            var Q152;
            Q152=makeQuery(id+"F5.boolean.opBoolean","SPLIT",FACE,{"disambiguationData":[TD([makeQuery(id+"F5.opExtrude","SWEPT_FACE",FACE,{"disambiguationData":[OSD([sQuery(id+"F4.wireOp",EDGE,"E10.sketch_text.stroke-119")])]})])],"derivedFrom":makeQuery(id+"F1.opExtrude","CAP_FACE",FACE,{"disambiguationData":[OSD([sQuery(id+"F0.wireOp",EDGE,"E0.bottom"),sQuery(id+"F0.wireOp",EDGE,"E0.top"),sQuery(id+"F0.wireOp",EDGE,"E0.left"),sQuery(id+"F0.wireOp",EDGE,"E0.right"),sQuery(id+"F0.wireOp",EDGE,"E1"),sQuery(id+"F0.wireOp",EDGE,"E7.MirrorC"),sQuery(id+"F0.wireOp",EDGE,"E8.MirrorC"),sQuery(id+"F0.wireOp",EDGE,"E9.MirrorC")])],"isStart":true})});
            var Q153;
            Q153=makeQuery(id+"F5.boolean.opBoolean","SPLIT",FACE,{"disambiguationData":[TD([makeQuery(id+"F5.opExtrude","SWEPT_FACE",FACE,{"disambiguationData":[OSD([sQuery(id+"F4.wireOp",EDGE,"E10.sketch_text.stroke-158")])]})])],"derivedFrom":makeQuery(id+"F1.opExtrude","CAP_FACE",FACE,{"disambiguationData":[OSD([sQuery(id+"F0.wireOp",EDGE,"E0.bottom"),sQuery(id+"F0.wireOp",EDGE,"E0.top"),sQuery(id+"F0.wireOp",EDGE,"E0.left"),sQuery(id+"F0.wireOp",EDGE,"E0.right"),sQuery(id+"F0.wireOp",EDGE,"E1"),sQuery(id+"F0.wireOp",EDGE,"E7.MirrorC"),sQuery(id+"F0.wireOp",EDGE,"E8.MirrorC"),sQuery(id+"F0.wireOp",EDGE,"E9.MirrorC")])],"isStart":true})});
            var Q154;
            Q154=makeQuery(id+"F5.opExtrude","SWEPT_FACE",FACE,{"disambiguationData":[OSD([sQuery(id+"F4.wireOp",EDGE,"E10.sketch_text.stroke-9")])]});
            var Q155;
            Q155=makeQuery(id+"F5.opExtrude","SWEPT_FACE",FACE,{"disambiguationData":[OSD([sQuery(id+"F4.wireOp",EDGE,"E10.sketch_text.stroke-167")])]});
            var Q156;
            Q156=makeQuery(id+"F5.opExtrude","SWEPT_FACE",FACE,{"disambiguationData":[OSD([sQuery(id+"F4.wireOp",EDGE,"E10.sketch_text.stroke-95")])]});
            var Q157;
            Q157=makeQuery(id+"F5.opExtrude","SWEPT_FACE",FACE,{"disambiguationData":[OSD([sQuery(id+"F4.wireOp",EDGE,"E10.sketch_text.stroke-184")])]});
            var Q158;
            Q158=makeQuery(id+"F5.opExtrude","SWEPT_FACE",FACE,{"disambiguationData":[OSD([sQuery(id+"F4.wireOp",EDGE,"E10.sketch_text.stroke-84")])]});
            var Q159;
            Q159=makeQuery(id+"F5.opExtrude","SWEPT_FACE",FACE,{"disambiguationData":[OSD([sQuery(id+"F4.wireOp",EDGE,"E10.sketch_text.stroke-68")])]});
            var Q160;
            Q160=makeQuery(id+"F5.opExtrude","SWEPT_FACE",FACE,{"disambiguationData":[OSD([sQuery(id+"F4.wireOp",EDGE,"E10.sketch_text.stroke-143")])]});
            var Q161;
            Q161=makeQuery(id+"F5.opExtrude","SWEPT_FACE",FACE,{"disambiguationData":[OSD([sQuery(id+"F4.wireOp",EDGE,"E10.sketch_text.stroke-189")])]});
            var Q162;
            Q162=makeQuery(id+"F5.opExtrude","CAP_FACE",FACE,{"disambiguationData":[OSD([sQuery(id+"F4.wireOp",EDGE,"E10.sketch_text.stroke-13"),sQuery(id+"F4.wireOp",EDGE,"E10.sketch_text.stroke-14"),sQuery(id+"F4.wireOp",EDGE,"E10.sketch_text.stroke-15"),sQuery(id+"F4.wireOp",EDGE,"E10.sketch_text.stroke-16"),sQuery(id+"F4.wireOp",EDGE,"E10.sketch_text.stroke-17"),sQuery(id+"F4.wireOp",EDGE,"E10.sketch_text.stroke-18"),sQuery(id+"F4.wireOp",EDGE,"E10.sketch_text.stroke-19"),sQuery(id+"F4.wireOp",EDGE,"E10.sketch_text.stroke-20")])],"isStart":false});
            var Q163;
            Q163=makeQuery(id+"F5.opExtrude","SWEPT_FACE",FACE,{"disambiguationData":[OSD([sQuery(id+"F4.wireOp",EDGE,"E10.sketch_text.stroke-57")])]});
            var Q164;
            Q164=makeQuery(id+"F5.opExtrude","SWEPT_FACE",FACE,{"disambiguationData":[OSD([sQuery(id+"F4.wireOp",EDGE,"E10.sketch_text.stroke-29")])]});
            var Q165;
            Q165=makeQuery(id+"F5.opExtrude","SWEPT_FACE",FACE,{"disambiguationData":[OSD([sQuery(id+"F4.wireOp",EDGE,"E10.sketch_text.stroke-60")])]});
            var Q166;
            Q166=makeQuery(id+"F5.opExtrude","SWEPT_FACE",FACE,{"disambiguationData":[OSD([sQuery(id+"F4.wireOp",EDGE,"E10.sketch_text.stroke-148")])]});
            var Q167;
            Q167=makeQuery(id+"F5.opExtrude","SWEPT_FACE",FACE,{"disambiguationData":[OSD([sQuery(id+"F4.wireOp",EDGE,"E10.sketch_text.stroke-75")])]});
            var Q168;
            Q168=makeQuery(id+"F5.opExtrude","SWEPT_FACE",FACE,{"disambiguationData":[OSD([sQuery(id+"F4.wireOp",EDGE,"E10.sketch_text.stroke-91")])]});
            var Q169;
            Q169=makeQuery(id+"F5.opExtrude","SWEPT_FACE",FACE,{"disambiguationData":[OSD([sQuery(id+"F4.wireOp",EDGE,"E10.sketch_text.stroke-78")])]});
            var Q170;
            Q170=makeQuery(id+"F5.opExtrude","SWEPT_FACE",FACE,{"disambiguationData":[OSD([sQuery(id+"F4.wireOp",EDGE,"E10.sketch_text.stroke-62")])]});
            var Q171;
            Q171=makeQuery(id+"F5.opExtrude","SWEPT_FACE",FACE,{"disambiguationData":[OSD([sQuery(id+"F4.wireOp",EDGE,"E10.sketch_text.stroke-182")])]});
            var Q172;
            Q172=makeQuery(id+"F5.opExtrude","SWEPT_FACE",FACE,{"disambiguationData":[OSD([sQuery(id+"F4.wireOp",EDGE,"E10.sketch_text.stroke-11")])]});
            var Q173;
            Q173=makeQuery(id+"F5.opExtrude","SWEPT_FACE",FACE,{"disambiguationData":[OSD([sQuery(id+"F4.wireOp",EDGE,"E10.sketch_text.stroke-97")])]});
            var Q174;
            Q174=makeQuery(id+"F5.opExtrude","SWEPT_FACE",FACE,{"disambiguationData":[OSD([sQuery(id+"F4.wireOp",EDGE,"E10.sketch_text.stroke-23")])]});
            var Q175;
            Q175=makeQuery(id+"F5.opExtrude","SWEPT_FACE",FACE,{"disambiguationData":[OSD([sQuery(id+"F4.wireOp",EDGE,"E10.sketch_text.stroke-80")])]});
            var Q176;
            Q176=makeQuery(id+"F5.boolean.opBoolean","SPLIT",FACE,{"disambiguationData":[TD([makeQuery(id+"F5.opExtrude","SWEPT_FACE",FACE,{"disambiguationData":[OSD([sQuery(id+"F4.wireOp",EDGE,"E10.sketch_text.stroke-99")])]})])],"derivedFrom":makeQuery(id+"F1.opExtrude","CAP_FACE",FACE,{"disambiguationData":[OSD([sQuery(id+"F0.wireOp",EDGE,"E0.bottom"),sQuery(id+"F0.wireOp",EDGE,"E0.top"),sQuery(id+"F0.wireOp",EDGE,"E0.left"),sQuery(id+"F0.wireOp",EDGE,"E0.right"),sQuery(id+"F0.wireOp",EDGE,"E1"),sQuery(id+"F0.wireOp",EDGE,"E7.MirrorC"),sQuery(id+"F0.wireOp",EDGE,"E8.MirrorC"),sQuery(id+"F0.wireOp",EDGE,"E9.MirrorC")])],"isStart":true})});
            var Q177;
            Q177=makeQuery(id+"F5.opExtrude","SWEPT_FACE",FACE,{"disambiguationData":[OSD([sQuery(id+"F4.wireOp",EDGE,"E10.sketch_text.stroke-168")])]});
            var Q178;
            Q178=makeQuery(id+"F5.opExtrude","SWEPT_FACE",FACE,{"disambiguationData":[OSD([sQuery(id+"F4.wireOp",EDGE,"E10.sketch_text.stroke-188")])]});
            var Q179;
            Q179=makeQuery(id+"F5.opExtrude","SWEPT_FACE",FACE,{"disambiguationData":[OSD([sQuery(id+"F4.wireOp",EDGE,"E10.sketch_text.stroke-129")])]});
            var Q180;
            Q180=makeQuery(id+"F5.opExtrude","SWEPT_FACE",FACE,{"disambiguationData":[OSD([sQuery(id+"F4.wireOp",EDGE,"E10.sketch_text.stroke-27")])]});
            var Q181;
            Q181=makeQuery(id+"F5.opExtrude","SWEPT_FACE",FACE,{"disambiguationData":[OSD([sQuery(id+"F4.wireOp",EDGE,"E10.sketch_text.stroke-175")])]});
            var Q182;
            Q182=makeQuery(id+"F5.opExtrude","SWEPT_FACE",FACE,{"disambiguationData":[OSD([sQuery(id+"F4.wireOp",EDGE,"E10.sketch_text.stroke-42")])]});
            var Q183;
            Q183=makeQuery(id+"F5.opExtrude","SWEPT_FACE",FACE,{"disambiguationData":[OSD([sQuery(id+"F4.wireOp",EDGE,"E10.sketch_text.stroke-118")])]});
            var Q184;
            Q184=makeQuery(id+"F5.opExtrude","SWEPT_FACE",FACE,{"disambiguationData":[OSD([sQuery(id+"F4.wireOp",EDGE,"E10.sketch_text.stroke-151")])]});
            var Q185;
            Q185=makeQuery(id+"F5.opExtrude","SWEPT_FACE",FACE,{"disambiguationData":[OSD([sQuery(id+"F4.wireOp",EDGE,"E10.sketch_text.stroke-137")])]});
            var Q186;
            Q186=makeQuery(id+"F5.opExtrude","SWEPT_FACE",FACE,{"disambiguationData":[OSD([sQuery(id+"F4.wireOp",EDGE,"E10.sketch_text.stroke-83")])]});
            var Q187;
            Q187=makeQuery(id+"F5.boolean.opBoolean","SPLIT",FACE,{"disambiguationData":[TD([makeQuery(id+"F5.opExtrude","SWEPT_FACE",FACE,{"disambiguationData":[OSD([sQuery(id+"F4.wireOp",EDGE,"E10.sketch_text.stroke-90")])]})])],"derivedFrom":makeQuery(id+"F1.opExtrude","CAP_FACE",FACE,{"disambiguationData":[OSD([sQuery(id+"F0.wireOp",EDGE,"E0.bottom"),sQuery(id+"F0.wireOp",EDGE,"E0.top"),sQuery(id+"F0.wireOp",EDGE,"E0.left"),sQuery(id+"F0.wireOp",EDGE,"E0.right"),sQuery(id+"F0.wireOp",EDGE,"E1"),sQuery(id+"F0.wireOp",EDGE,"E7.MirrorC"),sQuery(id+"F0.wireOp",EDGE,"E8.MirrorC"),sQuery(id+"F0.wireOp",EDGE,"E9.MirrorC")])],"isStart":true})});
            var Q188;
            Q188=makeQuery(id+"F5.opExtrude","SWEPT_FACE",FACE,{"disambiguationData":[OSD([sQuery(id+"F4.wireOp",EDGE,"E10.sketch_text.stroke-139")])]});
            var Q189;
            Q189=makeQuery(id+"F5.opExtrude","SWEPT_FACE",FACE,{"disambiguationData":[OSD([sQuery(id+"F4.wireOp",EDGE,"E10.sketch_text.stroke-70")])]});
            var Q190;
            Q190=makeQuery(id+"F5.opExtrude","SWEPT_FACE",FACE,{"disambiguationData":[OSD([sQuery(id+"F4.wireOp",EDGE,"E10.sketch_text.stroke-160")])]});
            var Q191;
            Q191=makeQuery(id+"F5.opExtrude","SWEPT_FACE",FACE,{"disambiguationData":[OSD([sQuery(id+"F4.wireOp",EDGE,"E10.sketch_text.stroke-71")])]});
            var Q192;
            Q192=makeQuery(id+"F5.opExtrude","SWEPT_FACE",FACE,{"disambiguationData":[OSD([sQuery(id+"F4.wireOp",EDGE,"E10.sketch_text.stroke-117")])]});
            var Q193;
            Q193=makeQuery(id+"F5.opExtrude","SWEPT_FACE",FACE,{"disambiguationData":[OSD([sQuery(id+"F4.wireOp",EDGE,"E10.sketch_text.stroke-147")])]});
            var Q194;
            Q194=makeQuery(id+"F5.opExtrude","SWEPT_FACE",FACE,{"disambiguationData":[OSD([sQuery(id+"F4.wireOp",EDGE,"E10.sketch_text.stroke-164")])]});
            var Q195;
            Q195=makeQuery(id+"F5.opExtrude","SWEPT_FACE",FACE,{"disambiguationData":[OSD([sQuery(id+"F4.wireOp",EDGE,"E10.sketch_text.stroke-61")])]});
            var Q196;
            Q196=makeQuery(id+"F5.opExtrude","SWEPT_FACE",FACE,{"disambiguationData":[OSD([sQuery(id+"F4.wireOp",EDGE,"E10.sketch_text.stroke-19")])]});
            var Q197;
            Q197=makeQuery(id+"F5.opExtrude","SWEPT_FACE",FACE,{"disambiguationData":[OSD([sQuery(id+"F4.wireOp",EDGE,"E10.sketch_text.stroke-35")])]});
            var Q198;
            Q198=makeQuery(id+"F5.opExtrude","SWEPT_FACE",FACE,{"disambiguationData":[OSD([sQuery(id+"F4.wireOp",EDGE,"E10.sketch_text.stroke-140")])]});
            var Q199;
            Q199=makeQuery(id+"F5.opExtrude","SWEPT_FACE",FACE,{"disambiguationData":[OSD([sQuery(id+"F4.wireOp",EDGE,"E10.sketch_text.stroke-20")])]});
            var Q200;
            Q200=makeQuery(id+"F5.opExtrude","SWEPT_FACE",FACE,{"disambiguationData":[OSD([sQuery(id+"F4.wireOp",EDGE,"E10.sketch_text.stroke-16")])]});
            var Q201;
            Q201=makeQuery(id+"F5.opExtrude","SWEPT_FACE",FACE,{"disambiguationData":[OSD([sQuery(id+"F4.wireOp",EDGE,"E10.sketch_text.stroke-18")])]});
            var Q202;
            Q202=makeQuery(id+"F5.opExtrude","SWEPT_FACE",FACE,{"disambiguationData":[OSD([sQuery(id+"F4.wireOp",EDGE,"E10.sketch_text.stroke-17")])]});
            var Q203;
            Q203=qCreatedBy(makeId("Right.planeOp"),FACE);
            mirror(context, id + "F6", {"operationType" : NewBodyOperationType.ADD, "entities" : qUnion([Q0]), "faces" : qUnion([Q1, Q2, Q3, Q4, Q5, Q6, Q7, Q8, Q9, Q10, Q11, Q12, Q13, Q14, Q15, Q16, Q17, Q18, Q19, Q20, Q21, Q22, Q23, Q24, Q25, Q26, Q27, Q28, Q29, Q30, Q31, Q32, Q33, Q34, Q35, Q36, Q37, Q38, Q39, Q40, Q41, Q42, Q43, Q44, Q45, Q46, Q47, Q48, Q49, Q50, Q51, Q52, Q53, Q54, Q55, Q56, Q57, Q58, Q59, Q60, Q61, Q62, Q63, Q64, Q65, Q66, Q67, Q68, Q69, Q70, Q71, Q72, Q73, Q74, Q75, Q76, Q77, Q78, Q79, Q80, Q81, Q82, Q83, Q84, Q85, Q86, Q87, Q88, Q89, Q90, Q91, Q92, Q93, Q94, Q95, Q96, Q97, Q98, Q99, Q100, Q101, Q102, Q103, Q104, Q105, Q106, Q107, Q108, Q109, Q110, Q111, Q112, Q113, Q114, Q115, Q116, Q117, Q118, Q119, Q120, Q121, Q122, Q123, Q124, Q125, Q126, Q127, Q128, Q129, Q130, Q131, Q132, Q133, Q134, Q135, Q136, Q137, Q138, Q139, Q140, Q141, Q142, Q143, Q144, Q145, Q146, Q147, Q148, Q149, Q150, Q151, Q152, Q153, Q154, Q155, Q156, Q157, Q158, Q159, Q160, Q161, Q162, Q163, Q164, Q165, Q166, Q167, Q168, Q169, Q170, Q171, Q172, Q173, Q174, Q175, Q176, Q177, Q178, Q179, Q180, Q181, Q182, Q183, Q184, Q185, Q186, Q187, Q188, Q189, Q190, Q191, Q192, Q193, Q194, Q195, Q196, Q197, Q198, Q199, Q200, Q201, Q202]), "mirrorPlane" : qUnion([Q203])});
        }
    });
